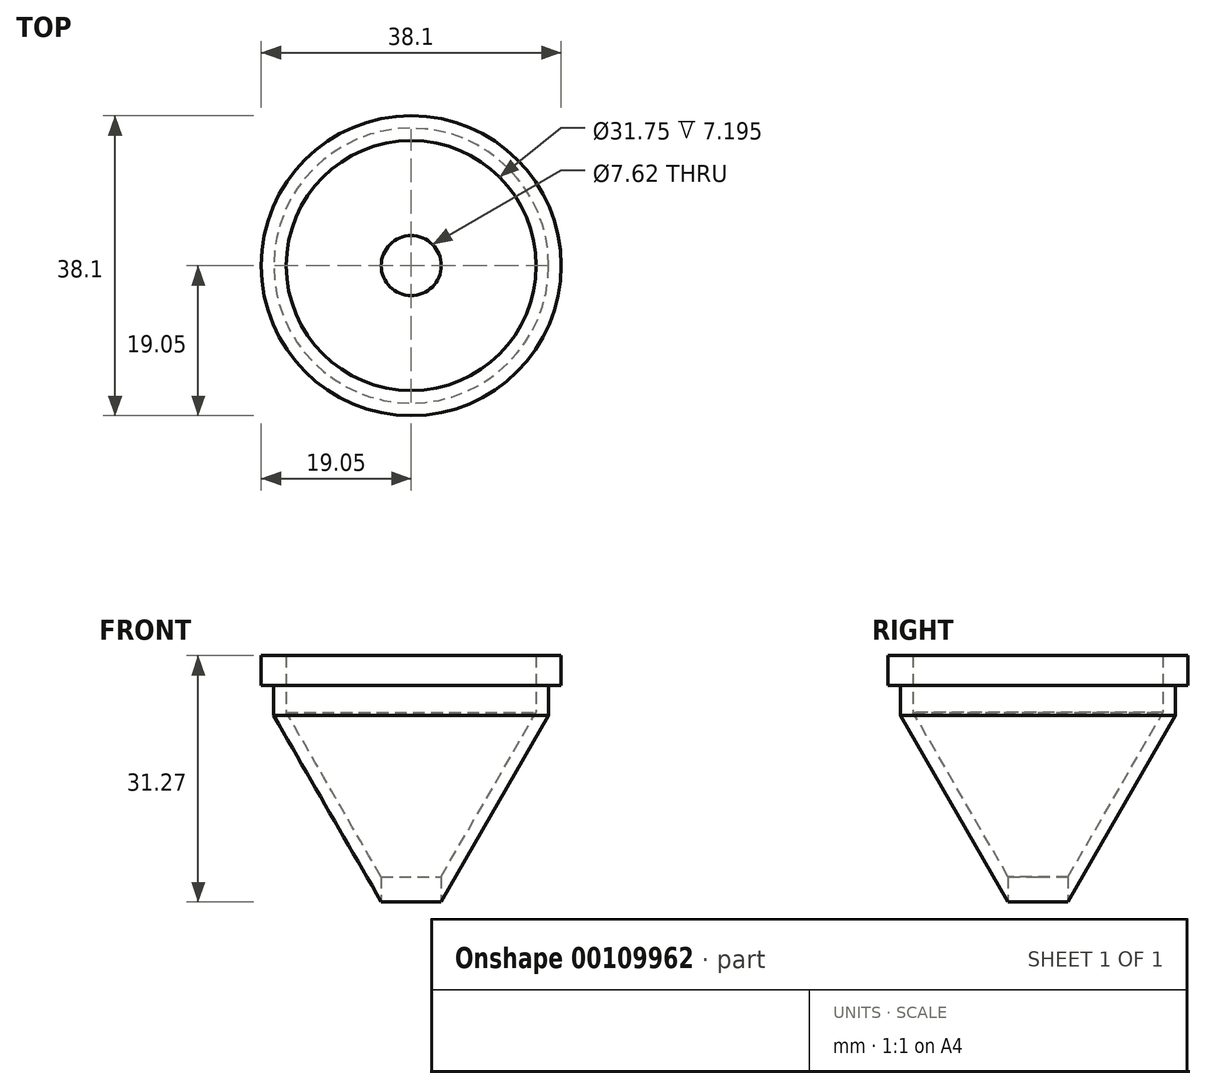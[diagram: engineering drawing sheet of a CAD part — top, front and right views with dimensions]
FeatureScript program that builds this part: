
annotation { "Feature Type Name" : "Feature", "Feature Type Description" : "" }
export const myFeature = defineFeature(function(context is Context, id is Id, definition is map)
    precondition{}
    {
        {
            var Q0;
            Q0=qCreatedBy(makeId("Front.planeOp"),FACE);
            var sketch = newSketch(context, id + "F0", { "sketchPlane" : qUnion([Q0])});
            skLineSegment(sketch, "E0", {"start": v(0, 0) * mm, "end": v(0, 41.3) * mm, "construction": true});
            skLineSegment(sketch, "E1", {"start": v(19.05, 29.21) * mm, "end": v(19.05, 25.4) * mm});
            skLineSegment(sketch, "E2", {"start": v(19.05, 25.4) * mm, "end": v(17.46, 25.4) * mm});
            skLineSegment(sketch, "E3", {"start": v(17.46, 25.4) * mm, "end": v(17.46, 21.59) * mm});
            skLineSegment(sketch, "E4", {"start": v(17.46, 21.59) * mm, "end": v(3.81, -2.06) * mm});
            skLineSegment(sketch, "E5", {"start": v(0, 0) * mm, "end": v(3.81, 0) * mm, "construction": true});
            skLineSegment(sketch, "E6", {"start": v(3.81, -2.06) * mm, "end": v(3.81, 1.12) * mm});
            skLineSegment(sketch, "E7", {"start": v(3.81, 1.12) * mm, "end": v(15.88, 22.02) * mm});
            skLineSegment(sketch, "E8", {"start": v(19.05, 29.21) * mm, "end": v(15.88, 29.21) * mm});
            skLineSegment(sketch, "E9", {"start": v(15.88, 29.21) * mm, "end": v(15.88, 22.02) * mm});
            skSolve(sketch);
        }
        {
            var Q0;
            Q0=makeQuery(id+"F0.imprint","IMPRINT",FACE,{"disambiguationData":[TD([[makeQuery(id+"F0.imprint","IMPRINT",EDGE,{"derivedFrom":sQuery(id+"F0.wireOp",EDGE,"E1")}),-1.0]])]});
            var Q1;
            Q1=sQuery(id+"F0.wireOp",EDGE,"E0");
            revolve(context, id + "F1", {"entities" : qUnion([Q0]), "axis" : qUnion([Q1]), "revolveType" : RevolveType.FULL});
        }
    });
